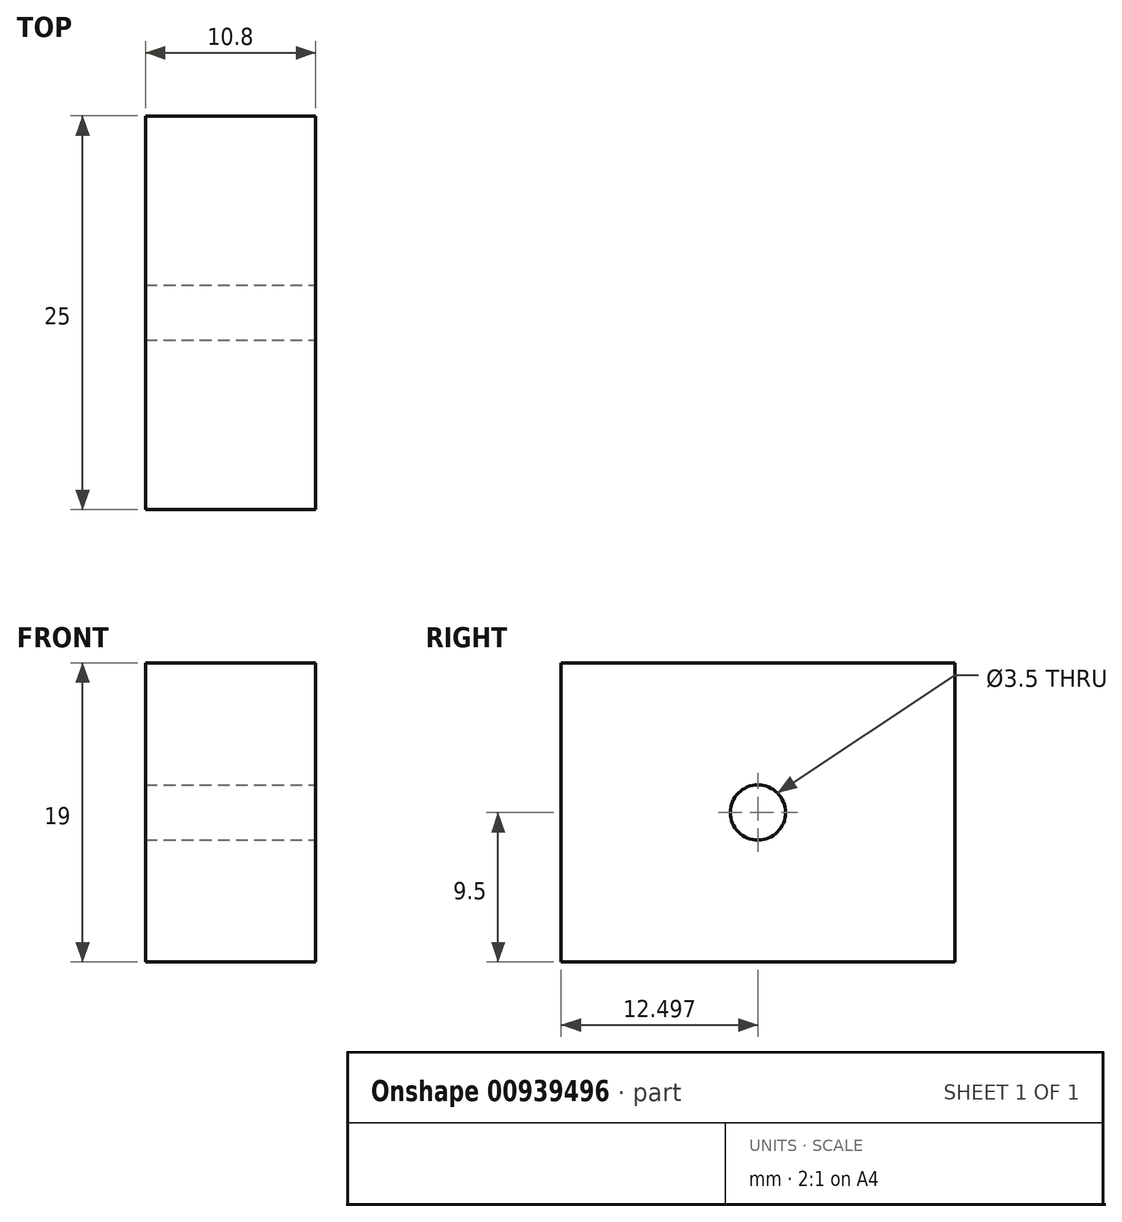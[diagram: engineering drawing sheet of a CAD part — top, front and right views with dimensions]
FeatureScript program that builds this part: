
annotation { "Feature Type Name" : "Feature", "Feature Type Description" : "" }
export const myFeature = defineFeature(function(context is Context, id is Id, definition is map)
    precondition{}
    {
        {
            var Q0;
            Q0=qCreatedBy(makeId("Top.planeOp"),FACE);
            var sketch = newSketch(context, id + "F0", { "sketchPlane" : qUnion([Q0])});
            skLineSegment(sketch, "E0.bottom", {"start": v(-7.1, -7.08) * mm, "end": v(3.7, -7.08) * mm});
            skLineSegment(sketch, "E0.top", {"start": v(-7.1, -32.08) * mm, "end": v(3.7, -32.08) * mm});
            skLineSegment(sketch, "E0.left", {"start": v(-7.1, -7.08) * mm, "end": v(-7.1, -32.08) * mm});
            skLineSegment(sketch, "E0.right", {"start": v(3.7, -7.08) * mm, "end": v(3.7, -32.08) * mm});
            skSolve(sketch);
        }
        {
            var Q0;
            Q0=makeQuery(id+"F0.imprint","IMPRINT",FACE,{"disambiguationData":[TD([[makeQuery(id+"F0.imprint","IMPRINT",EDGE,{"derivedFrom":sQuery(id+"F0.wireOp",EDGE,"E0.bottom")}),-1.0]])]});
            extrude(context, id + "F1", {"entities" : qUnion([Q0]), "depth" : 19 * mm, "offsetDistance" : 25 * mm});
        }
        {
            var Q0;
            Q0=makeQuery(id+"F1.opExtrude","SWEPT_FACE",FACE,{"disambiguationData":[OSD([sQuery(id+"F0.wireOp",EDGE,"E0.right")])]});
            var sketch = newSketch(context, id + "F2", { "sketchPlane" : qUnion([Q0])});
            skPoint(sketch, "E1", {"position": v(-19.58, 9.5) * mm});
            skPoint(sketch, "E1.positionSnap0", {"position": v(-19.58, 19) * mm});
            skSolve(sketch);
        }
        {
            var Q0;
            Q0=sQuery(id+"F2.wireOp",VERTEX,"E1");
            var Q1;
            Q1=makeQuery(id+"F1.opExtrude","SWEPT_BODY",BODY,{"disambiguationData":[OSD([sQuery(id+"F0.wireOp",EDGE,"E0.bottom"),sQuery(id+"F0.wireOp",EDGE,"E0.top"),sQuery(id+"F0.wireOp",EDGE,"E0.left"),sQuery(id+"F0.wireOp",EDGE,"E0.right")])]});
            hole(context, id + "F3", {"style" : HoleStyle.SIMPLE, "endStyle" : HoleEndStyle.BLIND, "holeDiameter" : 3.5 * mm, "majorDiameter" : 5 * mm, "holeDepth" : 20 * mm, "isTappedThrough" : true, "tappedDepth" : 12 * mm, "tapClearance" : 3, "locations" : qUnion([Q0]), "scope" : qUnion([Q1])});
        }
    });
